# Revit family: DA_Клапан_Регулятор_КРК-ВД_VEOX
name_source: partatom
category: Арматура воздуховодов
units: mm (PartAtom-declared; Revit-internal decimal feet)

## family parameters
Всегда вертикально = Нет
На основе рабочей плоскости = Нет
Номер OmniClass = 23.33.41.17.13
Общий = Нет
При загрузке вырезать с полостями = Нет
Размер круглого соединителя = Использовать диаметр
Тип детали = Вставляется

## types (2) — shared parameters
ADSK_Дата изменения = 02.01.2023
ADSK_Единица измерения = шт.
ADSK_Завод-изготовитель = Veox
ADSK_Количество = 1
ADSK_Наименование краткое = Регулятор расхода воздуха
CSV = КРК-ВД
URL = https://veox.ru
КМС = 3.18
Корпус = Оцинкованная сталь
Лопатка = Оцинкованная сталь
Максимальный размер клапана = 400мм
Минимальный размер клапана = 80мм
Фланец = Оцинкованная сталь
Хомут быстросъемный = Да
zero-valued in all types: Отметка по умолчанию

## per-type parameters (varying)
| type | ADSK_Марка | ИЗОЛЯЦИЯ | сдвиг изоляции | тип |
| КРК-ВД DN80-400 (без изоляции) |  | Нет | 0 мм | 1 |
| КРК-ВД DN80-400 (c изоляцией) | КРК-ВД | Да | 50 мм | 2 |

## geometry (parser evidence)
native form markers: Sweep x2
no freeform markers — native parametric forms only
